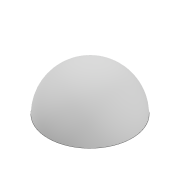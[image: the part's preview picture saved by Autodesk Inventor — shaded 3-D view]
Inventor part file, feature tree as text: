
AUTODESK INVENTOR PART (.ipt)
format: ipt  version: 2020 (Build 240168000, 168)  size: 99,840 bytes
history: native  units: mm
features: sketch x2, revolve x1, extrude x1
ambient origin geometry x8: Origin, YZ Plane, XZ Plane, XY Plane, X Axis, Y Axis, Z Axis, Center Point
bodies: Solid1 (feature_tree)
feature tree (4):
  revolve  "Revolution1"  [1 undecoded]
  extrude  "Extrusion1"  [1 undecoded]
  sketch  "Sketch1"  dims[d0=61.959188mm d1=30.5mm d2=0.0mm]
  sketch  "Sketch2"
note: 2 required parameter values undecoded (feature->parameter linkage not recoverable at this tier; creation-order binding heuristic only, values carry confidence <= 0.55)